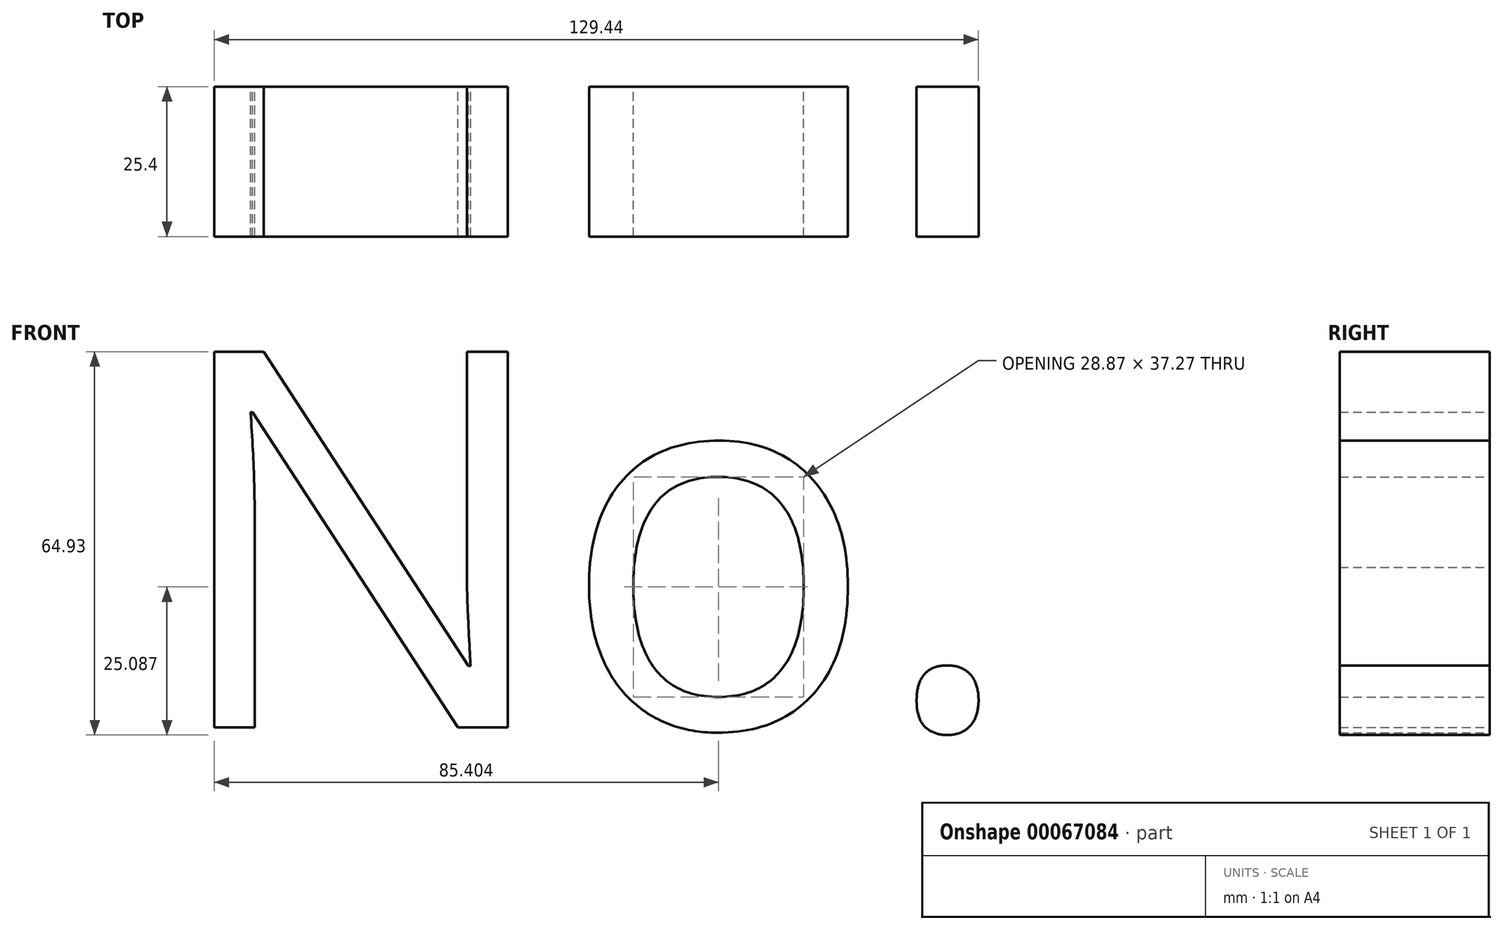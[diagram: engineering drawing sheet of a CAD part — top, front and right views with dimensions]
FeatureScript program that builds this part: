
annotation { "Feature Type Name" : "Feature", "Feature Type Description" : "" }
export const myFeature = defineFeature(function(context is Context, id is Id, definition is map)
    precondition{}
    {
        {
            var Q0;
            Q0=qCreatedBy(makeId("Front.planeOp"),FACE);
            var sketch = newSketch(context, id + "F0", { "sketchPlane" : qUnion([Q0])});
            skText(sketch, "E0", { "text": "No.\n", "fontName": "OpenSans-Regular.ttf"});
            const initialGuessF0  = {"E0": [-0.05705, -0.00575, 1, 0, 0.0642]};
            skSetInitialGuess(sketch, initialGuessF0);
            skSolve(sketch);
        }
        {
            var Q0;
            Q0=makeQuery(id+"F0.imprint","IMPRINT",FACE,{"disambiguationData":[TD([[makeQuery(id+"F0.imprint","IMPRINT",EDGE,{"derivedFrom":sQuery(id+"F0.wireOp",EDGE,"E0.sketch_text.stroke-15")}),-1.0]])]});
            extrude(context, id + "F1", {"entities" : qUnion([Q0]), "depth" : 25.4 * mm});
        }
        {
            var Q0;
            Q0=makeQuery(id+"F0.imprint","IMPRINT",FACE,{"disambiguationData":[TD([[makeQuery(id+"F0.imprint","IMPRINT",EDGE,{"derivedFrom":sQuery(id+"F0.wireOp",EDGE,"E0.sketch_text.stroke-0")}),-1.0]])]});
            extrude(context, id + "F2", {"entities" : qUnion([Q0]), "depth" : 25.4 * mm});
        }
        {
            var Q0;
            Q0=makeQuery(id+"F0.imprint","IMPRINT",FACE,{"disambiguationData":[TD([[makeQuery(id+"F0.imprint","IMPRINT",EDGE,{"derivedFrom":sQuery(id+"F0.wireOp",EDGE,"E0.sketch_text.stroke-32")}),-1.0]])]});
            extrude(context, id + "F3", {"entities" : qUnion([Q0]), "depth" : 25.4 * mm});
        }
    });
